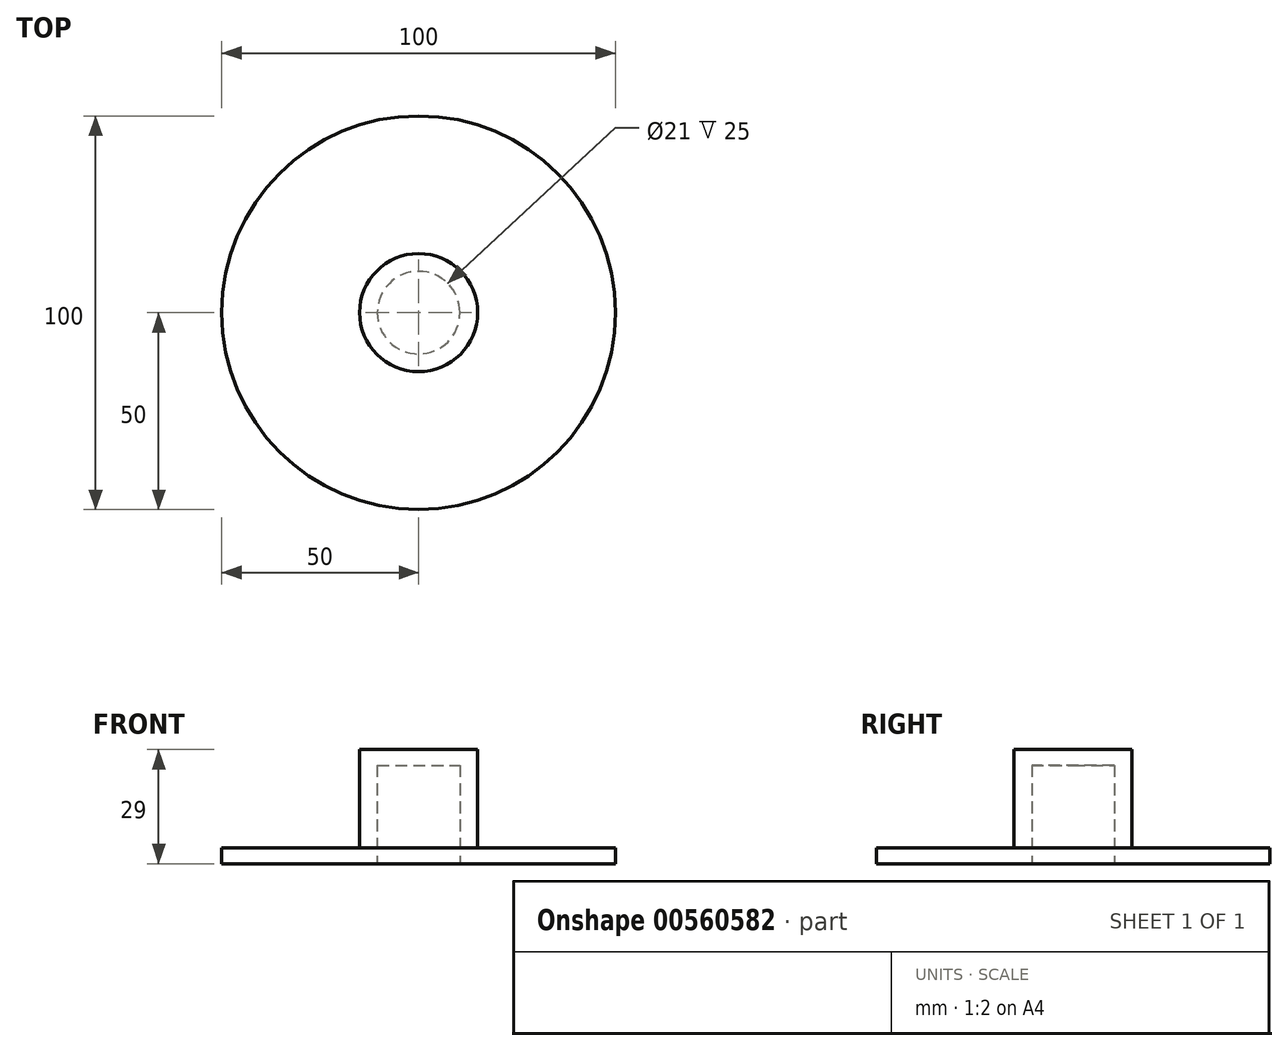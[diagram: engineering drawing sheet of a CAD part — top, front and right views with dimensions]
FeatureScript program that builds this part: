
annotation { "Feature Type Name" : "Feature", "Feature Type Description" : "" }
export const myFeature = defineFeature(function(context is Context, id is Id, definition is map)
    precondition{}
    {
        {
            var Q0;
            Q0=qCreatedBy(makeId("Top.planeOp"),FACE);
            var sketch = newSketch(context, id + "F0", { "sketchPlane" : qUnion([Q0])});
            skCircle(sketch, "E0", {"center": v(0, 0) * mm, "radius": 50 * mm});
            skSolve(sketch);
        }
        {
            var Q0;
            Q0 = qSketchRegion(id + "F0", true);
            extrude(context, id + "F1", {"entities" : qUnion([Q0]), "depth" : 4 * mm, "offsetDistance" : 25 * mm});
        }
        {
            var Q0;
            Q0=makeQuery(id+"F1.opExtrude","CAP_FACE",FACE,{"disambiguationData":[OSD([sQuery(id+"F0.wireOp",EDGE,"E0")])],"isStart":false});
            var sketch = newSketch(context, id + "F2", { "sketchPlane" : qUnion([Q0])});
            skCircle(sketch, "E1", {"center": v(0, 0) * mm, "radius": 15 * mm});
            skSolve(sketch);
        }
        {
            var Q0;
            Q0 = qSketchRegion(id + "F2", true);
            extrude(context, id + "F3", {"entities" : qUnion([Q0]), "operationType" : NewBodyOperationType.ADD, "depth" : 25 * mm, "offsetDistance" : 25 * mm});
        }
        {
            var Q0;
            Q0=makeQuery(id+"F1.opExtrude","CAP_FACE",FACE,{"disambiguationData":[OSD([sQuery(id+"F0.wireOp",EDGE,"E0")])],"isStart":true});
            var sketch = newSketch(context, id + "F4", { "sketchPlane" : qUnion([Q0])});
            skCircle(sketch, "E2", {"center": v(0, 0) * mm, "radius": 10.5 * mm});
            skSolve(sketch);
        }
        {
            var Q0;
            Q0 = qSketchRegion(id + "F4", true);
            extrude(context, id + "F5", {"entities" : qUnion([Q0]), "operationType" : NewBodyOperationType.REMOVE, "oppositeDirection" : true, "depth" : 25 * mm, "offsetDistance" : 25 * mm});
        }
    });
